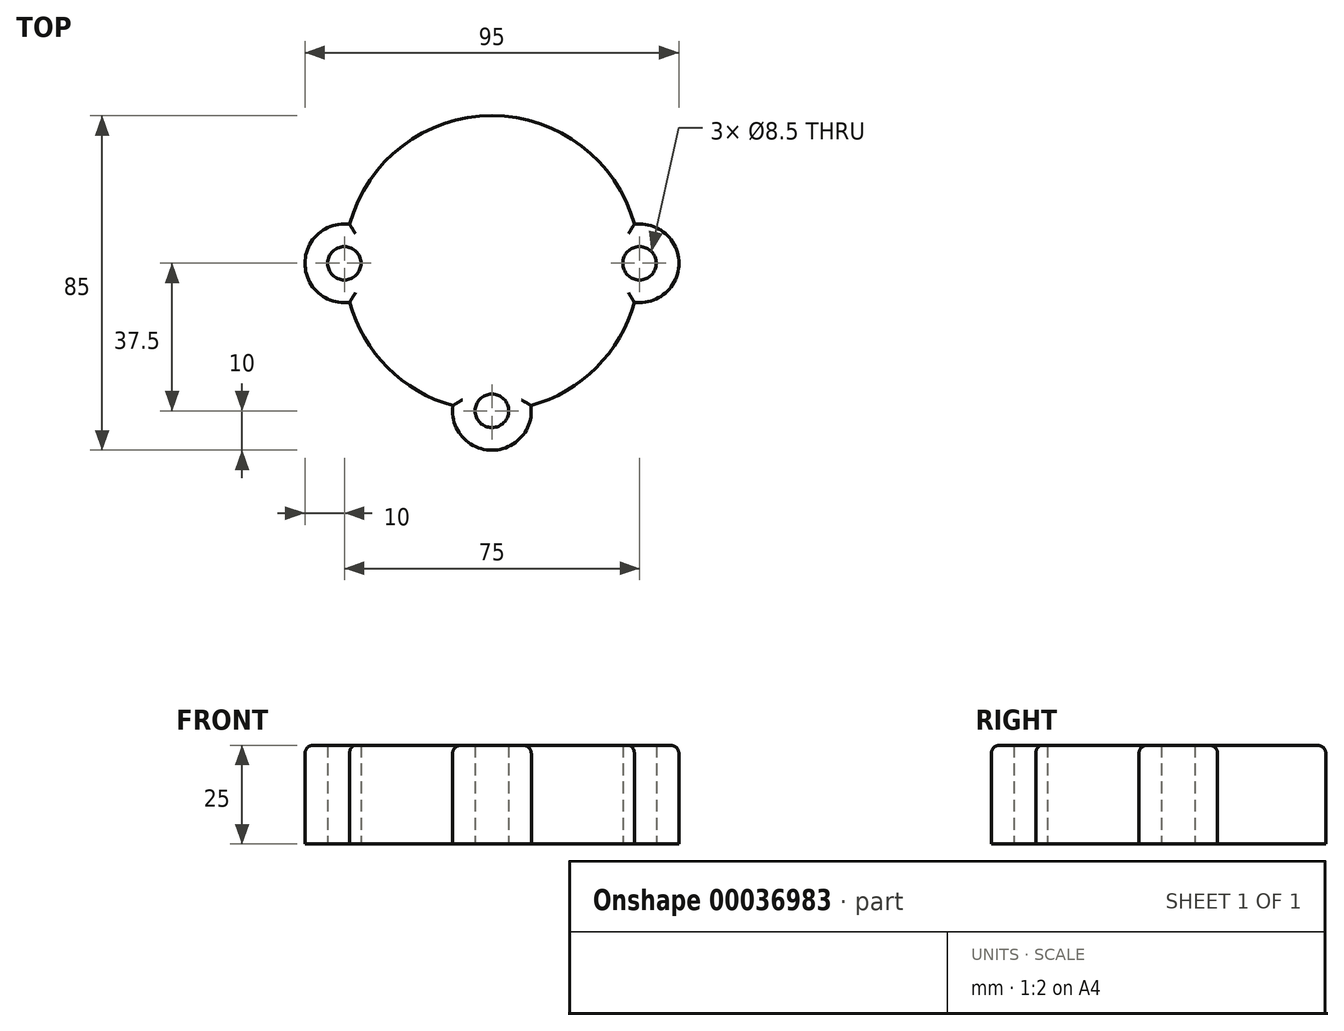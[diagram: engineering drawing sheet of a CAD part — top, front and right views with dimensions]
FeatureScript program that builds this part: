
annotation { "Feature Type Name" : "Feature", "Feature Type Description" : "" }
export const myFeature = defineFeature(function(context is Context, id is Id, definition is map)
    precondition{}
    {
        {
            var Q0;
            Q0=qCreatedBy(makeId("Top.planeOp"),FACE);
            var sketch = newSketch(context, id + "F0", { "sketchPlane" : qUnion([Q0])});
            skArc(sketch, "E0", {"start": v(36.17, 9.91) * mm, "mid": v(0, 37.5) * mm, "end": v(-36.17, 9.91) * mm});
            skArc(sketch, "E1", {"start": v(-9.91, -36.17) * mm, "mid": v(0, -47.5) * mm, "end": v(9.91, -36.17) * mm});
            skArc(sketch, "E2", {"start": v(36.17, -9.91) * mm, "mid": v(47.5, 0) * mm, "end": v(36.17, 9.91) * mm});
            skArc(sketch, "E3", {"start": v(-36.17, 9.91) * mm, "mid": v(-47.5, 0) * mm, "end": v(-36.17, -9.91) * mm});
            skArc(sketch, "E4.trimOffspring", {"start": v(9.91, -36.17) * mm, "mid": v(26.52, -26.52) * mm, "end": v(36.17, -9.91) * mm});
            skArc(sketch, "E5.trimOffspring", {"start": v(-36.17, -9.91) * mm, "mid": v(-26.52, -26.52) * mm, "end": v(-9.91, -36.17) * mm});
            skCircle(sketch, "E6", {"center": v(-37.5, 0) * mm, "radius": 4.25 * mm});
            skCircle(sketch, "E7", {"center": v(0, -37.5) * mm, "radius": 4.25 * mm});
            skCircle(sketch, "E8", {"center": v(37.5, 0) * mm, "radius": 4.25 * mm});
            skSolve(sketch);
        }
        {
            var Q0;
            Q0=makeQuery(id+"F0.imprint","IMPRINT",FACE,{"disambiguationData":[TD([[makeQuery(id+"F0.imprint","IMPRINT",EDGE,{"derivedFrom":sQuery(id+"F0.wireOp",EDGE,"E0")}),1.0]])]});
            extrude(context, id + "F1", {"entities" : qUnion([Q0]), "depth" : 25 * mm});
        }
        {
            var Q0;
            Q0=makeQuery(id+"F1.opExtrude","CAP_EDGE",EDGE,{"disambiguationData":[OSD([sQuery(id+"F0.wireOp",EDGE,"E5.trimOffspring")])],"isStart":false});
            var Q1;
            Q1=makeQuery(id+"F1.opExtrude","CAP_EDGE",EDGE,{"disambiguationData":[OSD([sQuery(id+"F0.wireOp",EDGE,"E4.trimOffspring")])],"isStart":false});
            var Q2;
            Q2=makeQuery(id+"F1.opExtrude","CAP_EDGE",EDGE,{"disambiguationData":[OSD([sQuery(id+"F0.wireOp",EDGE,"E2")])],"isStart":false});
            var Q3;
            Q3=makeQuery(id+"F1.opExtrude","CAP_EDGE",EDGE,{"disambiguationData":[OSD([sQuery(id+"F0.wireOp",EDGE,"E0")])],"isStart":false});
            var Q4;
            Q4=makeQuery(id+"F1.opExtrude","CAP_EDGE",EDGE,{"disambiguationData":[OSD([sQuery(id+"F0.wireOp",EDGE,"E3")])],"isStart":false});
            fillet(context, id + "F2", {"entities" : qUnion([Q0, Q1, Q2, Q3, Q4]), "radius" : 2 * mm, "tangentPropagation" : true, "allowEdgeOverflow" : false});
        }
        {
            var Q0;
            Q0=makeQuery(id+"F1.opExtrude","CAP_EDGE",EDGE,{"disambiguationData":[OSD([sQuery(id+"F0.wireOp",EDGE,"E1")])],"isStart":false});
            fillet(context, id + "F3", {"entities" : qUnion([Q0]), "radius" : 2 * mm, "tangentPropagation" : true, "allowEdgeOverflow" : false});
        }
    });
